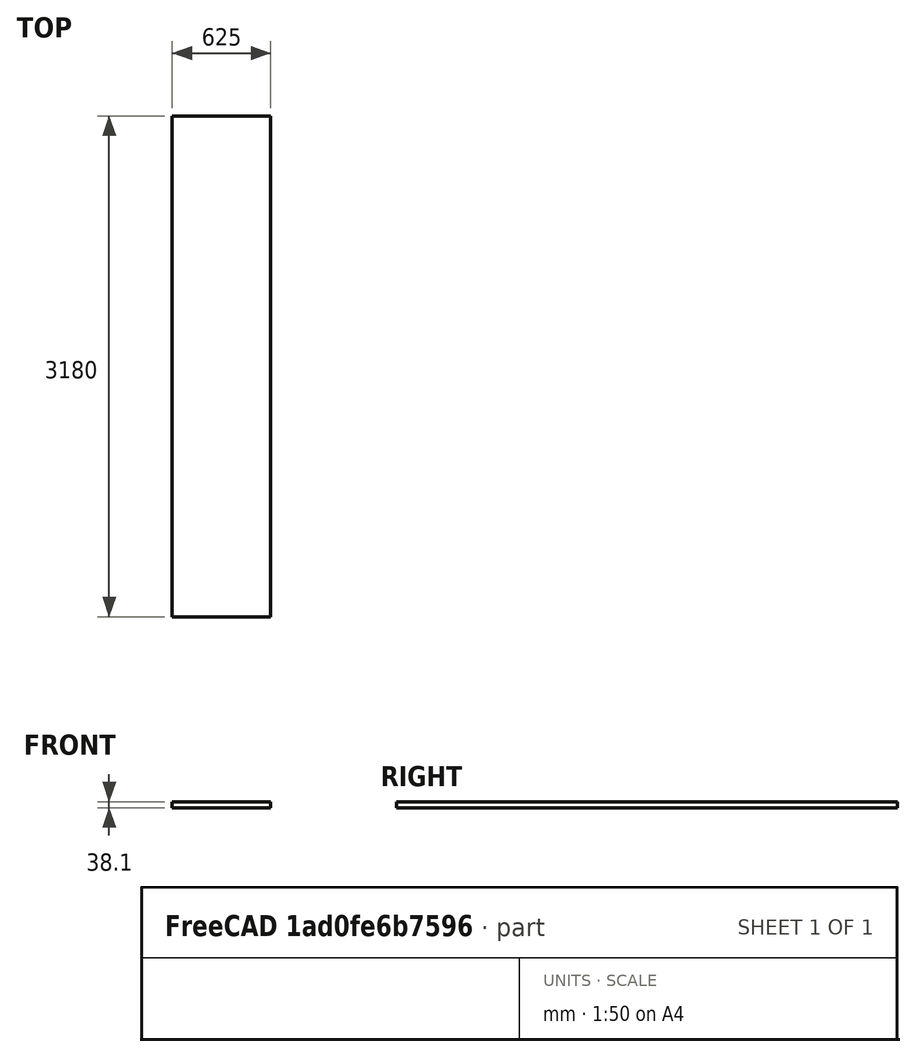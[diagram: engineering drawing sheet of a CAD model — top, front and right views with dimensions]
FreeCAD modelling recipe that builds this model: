
FCSTD DOCUMENT  (FreeCAD 0.19R24291 (Git))
Label: deskTop
License: All rights reserved
LicenseURL: http://en.wikipedia.org/wiki/All_rights_reserved
objects: Sketcher::SketchObject×1, PartDesign::Pad×1, PartDesign::Body×1
note: 4 computed .brp shape members not serialized (recipe doc carries the construction recipe); baked Part::Feature solids carry a one-line shape summary decoded from their .brp

FEATURE [Sketcher::SketchObject] Sketch
  FullyConstrained = true
  MapMode = 5
  Support = -> [XY_Plane]
  expr: Constraints[10] = 3130 + 25 + 25
  expr: Constraints[9] = 600 + 25
  sketch-geometry (4):
    g0: LineSegment StartX=0 StartY=0 StartZ=0 EndX=625 EndY=0 EndZ=0
    g1: LineSegment StartX=625 StartY=0 StartZ=0 EndX=625 EndY=-3180 EndZ=0
    g2: LineSegment StartX=625 StartY=-3180 StartZ=0 EndX=0 EndY=-3180 EndZ=0
    g3: LineSegment StartX=0 StartY=-3180 StartZ=0 EndX=0 EndY=0 EndZ=0
  constraints (11):
    c: Coincident(g0,g1)
    c: Coincident(g1,g2)
    c: Coincident(g2,g3)
    c: Coincident(g3,g0)
    c: Horizontal(g0)
    c: Horizontal(g2)
    c: Vertical(g1)
    c: Vertical(g3)
    c: Coincident(g0,g-1)
    c: DistanceX(g0,g0) = 625
    c: DistanceY(g3,g3) = 3180
FEATURE [PartDesign::Pad] Pad
  Direction = (1,1,1)
  Length = 38.1
  Length2 = 100
  Profile = -> Sketch
  Type = 0
  expr: Length = 1.5 * 25.4
FEATURE [PartDesign::Body] Body
  Group = -> [Sketch,Pad]
  Origin = -> Origin
  Tip = -> Pad
